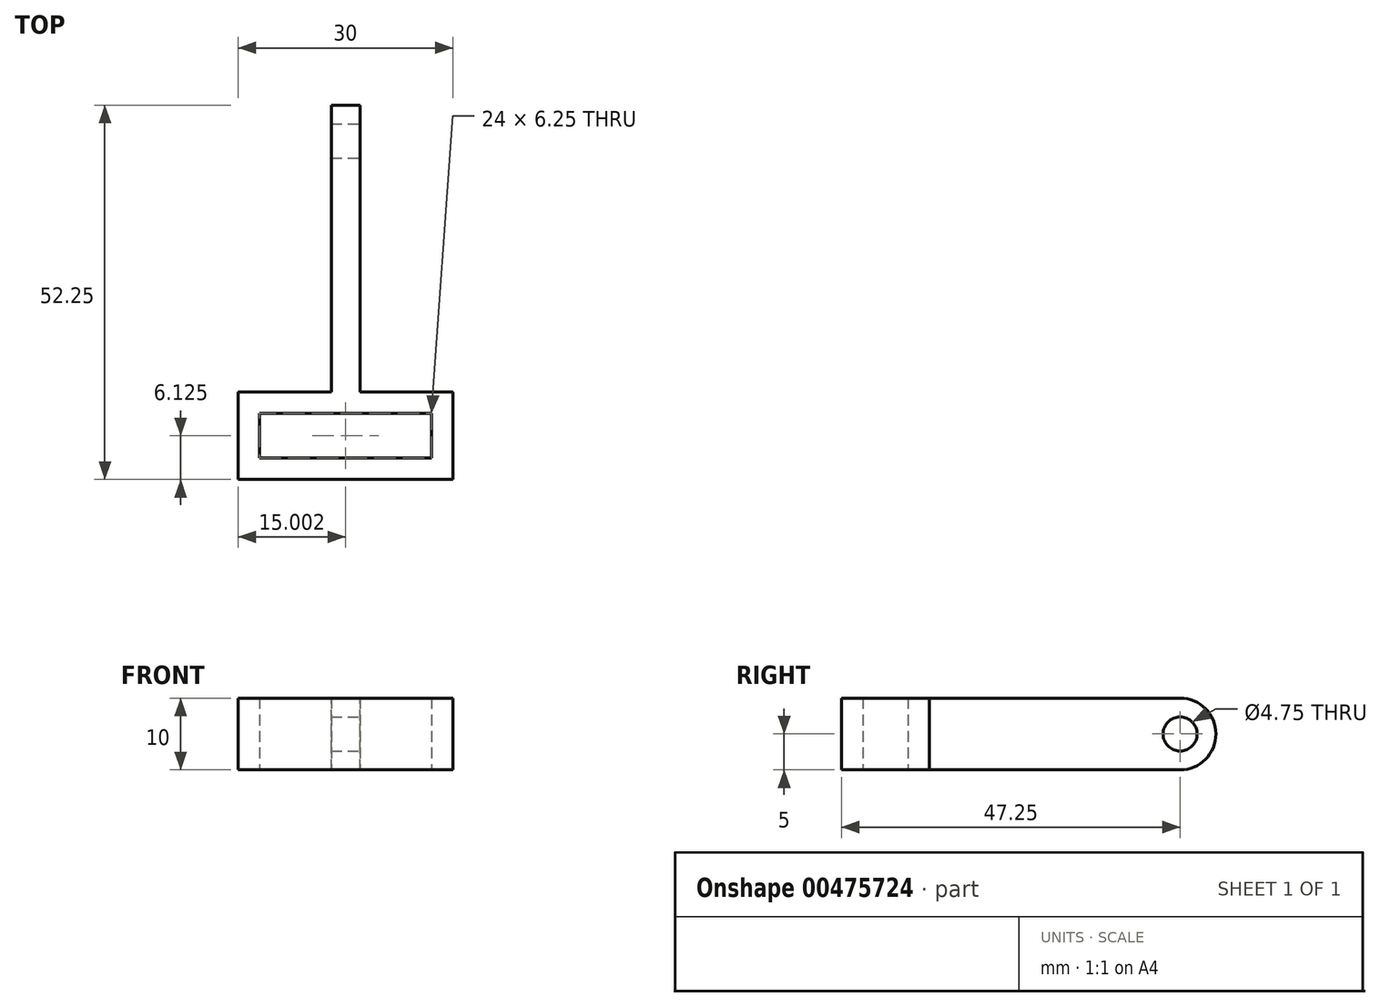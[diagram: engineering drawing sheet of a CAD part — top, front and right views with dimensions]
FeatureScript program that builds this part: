
annotation { "Feature Type Name" : "Feature", "Feature Type Description" : "" }
export const myFeature = defineFeature(function(context is Context, id is Id, definition is map)
    precondition{}
    {
        {
            var Q0;
            Q0=qCreatedBy(makeId("Top.planeOp"),FACE);
            var sketch = newSketch(context, id + "F0", { "sketchPlane" : qUnion([Q0])});
            skLineSegment(sketch, "E0.bottom", {"start": v(-12, 0) * mm, "end": v(12, 0) * mm});
            skLineSegment(sketch, "E0.top", {"start": v(-12, -6.25) * mm, "end": v(12, -6.25) * mm});
            skLineSegment(sketch, "E0.left", {"start": v(-12, 0) * mm, "end": v(-12, -6.25) * mm, "construction": true});
            skLineSegment(sketch, "E0.right", {"start": v(12, 0) * mm, "end": v(12, -6.25) * mm});
            skLineSegment(sketch, "E1", {"start": v(-12, -6.25) * mm, "end": v(-12, -9.25) * mm});
            skLineSegment(sketch, "E2", {"start": v(-12, -9.25) * mm, "end": v(15, -9.25) * mm});
            skLineSegment(sketch, "E3", {"start": v(15, -9.25) * mm, "end": v(15, 3) * mm});
            skLineSegment(sketch, "E4", {"start": v(12, -6.25) * mm, "end": v(15, -6.25) * mm});
            skLineSegment(sketch, "E5.bottom", {"start": v(-12, 3) * mm, "end": v(-15, 3) * mm});
            skLineSegment(sketch, "E5.top", {"start": v(-12, -9.25) * mm, "end": v(-15, -9.25) * mm});
            skLineSegment(sketch, "E5.left", {"start": v(-12, 3) * mm, "end": v(-12, -9.25) * mm});
            skLineSegment(sketch, "E5.right", {"start": v(-15, 3) * mm, "end": v(-15, -9.25) * mm});
            skLineSegment(sketch, "E6", {"start": v(-12, 3) * mm, "end": v(15, 3) * mm});
            skLineSegment(sketch, "E7.bottom", {"start": v(-2, 43) * mm, "end": v(2, 43) * mm});
            skLineSegment(sketch, "E7.top", {"start": v(-2, 3) * mm, "end": v(2, 3) * mm});
            skLineSegment(sketch, "E7.left", {"start": v(-2, 43) * mm, "end": v(-2, 3) * mm});
            skLineSegment(sketch, "E7.right", {"start": v(2, 43) * mm, "end": v(2, 3) * mm});
            skSolve(sketch);
        }
        {
            var Q0;
            Q0=qSketchRegion(id+"F0",true);
            extrude(context, id + "F1", {"entities" : qUnion([Q0]), "depth" : 10 * mm});
        }
        {
            var Q0;
            Q0=qCreatedBy(makeId("Right.planeOp"),FACE);
            var sketch = newSketch(context, id + "F2", { "sketchPlane" : qUnion([Q0])});
            skLineSegment(sketch, "E8.0", {"start": v(43, 10) * mm, "end": v(43, 0) * mm, "construction": true});
            skCircle(sketch, "E9", {"center": v(38, 5) * mm, "radius": 2.38 * mm});
            skPoint(sketch, "E9.centerSnap0", {"position": v(43, 5) * mm});
            skLineSegment(sketch, "E10", {"start": v(43, 5) * mm, "end": v(38, 5) * mm, "construction": true});
            skLineSegment(sketch, "E11", {"start": v(38, 0) * mm, "end": v(38, 5) * mm, "construction": true});
            skSolve(sketch);
        }
        {
            var Q0;
            Q0=qSketchRegion(id+"F2",true);
            extrude(context, id + "F3", {"entities" : qUnion([Q0]), "operationType" : NewBodyOperationType.REMOVE, "endBound" : BoundingType.SYMMETRIC, "oppositeDirection" : true, "depth" : 25 * mm});
        }
        {
            var Q0;
            Q0=makeQuery(id+"F1.opExtrude","CAP_EDGE",EDGE,{"disambiguationData":[OSD([sQuery(id+"F0.wireOp",EDGE,"E7.bottom")])],"isStart":false});
            var Q1;
            Q1=makeQuery(id+"F1.opExtrude","CAP_EDGE",EDGE,{"disambiguationData":[OSD([sQuery(id+"F0.wireOp",EDGE,"E7.bottom")])],"isStart":true});
            fillet(context, id + "F4", {"entities" : qUnion([Q0, Q1]), "radius" : 5 * mm, "tangentPropagation" : true, "allowEdgeOverflow" : false});
        }
    });
